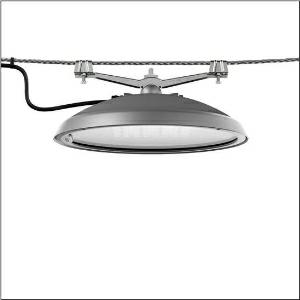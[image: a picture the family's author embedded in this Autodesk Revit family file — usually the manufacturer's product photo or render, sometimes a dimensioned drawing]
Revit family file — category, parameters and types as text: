
# Revit family: dl_r__50_iq_mini___st1_0s_5xa248w41f08re_89db
name_source: partatom
category: Lighting Fixtures
units: mm (PartAtom-declared; Revit-internal decimal feet)

## family parameters
Cut with Voids When Loaded = No
Host = Face
Light Source = No
Part Type = Normal
Room Calculation Point = No
Round Connector Dimension = Use Diameter
Shared = No

## types (1)
- --- (1 x LED, 5990 lm, 33.8 W, 4000K)
    Apparent Load = 34 VA
    CIE Flux Codes = 37 72 97 100 100
    Color Rendering = 70
    Color Temperature = 4000K
    Default Elevation = 1800 mm
    Description = DL® 50 iQ mini, catenary luminaire, primary light control with lens, of PMMA, primary optical cover: cover, of toughened safety glass, transparent, light distribution: ST1.0s, light emission: direct distribution, primary light characteristic: symmetric, installation type: suspended mounting, LED, High Power LED, rated luminous flux: 5.990lm, luminous efficacy: 177lm/W, light colour: 740, colour temperature: 4000K, control gear: iQ Street-Remote, control: optimised constant luminous flux control (CLO 2.0), Desk-Remote (wireless, voltage-free reading and setting of iQ features in the workshop via application-optimized NFC function/RFID function), Light-Fading, Smart-Wire, Night-Set, Lumen-Switch, Temp-Guard, Auto-Match, Street-Remote, mains connection: 230..240V, AC, 50/60Hz, start of lifetime: 34W, end of service life: 35W, reduction: 16W, luminaire housing, of diecast aluminium, powder-coated, Siteco® metallic grey (DB 702S), diameter: 500mm, height: 115mm, mounting height: 4..12m, protection rating (complete): IP66, insulation class (complete): insulation class II (safety insulation), certification: CE, ENEC, ENEC+, VDE, impact resistance: IK08, permissible operating ambient temperature for outdoor applications: -25..+40°C, standard-compliant lighting for roads and squares, packaging unit: 1 piece

Light Distribution: ST1.0s
    Height = 124 mm  [stored 0.406824 ft]
    Lamp = 1 x LED
    Lamp Light Flux = 5990 lm
    Lamp Power = 33.8 W
    Lamp count = 1
    Length = 500 mm
    Luminous efficacy = 177 lm/W
    Manufacturer = Siteco
    ModVariant = No
    Model = 5XA248W41F08RE
    Number of Poles = 1
    OnlyDefault = Yes
    Power Factor = 1
    Product Name = DL® 50 iQ mini | ST1.0s
    Product group = catenary luminaire
    ProductGroupID = 6300
    Protection Class = Protection class II
    Protection Degree = IP 66
    RLX_Detail_Level = 1
    RLX_Emergency_Light_Flux = 0 lm
    RLX_Emergency_Type = 0
    RLX_Emergency_Type_DB = No
    RlxData = <blob elided: 123845 chars, md5=371a3253>
    Socket = socket
    Standby Power = 0 W
    System Light Flux = 5990 lm
    System Power = 34 W
    Type Comments = factory setting: luminous flux: 100 % | dim-lin: 254 | 359 mA
    Type Image = l_1242791.jpg
    URL = http://relux.com
    VarID = @adj_140716
    Voltage = 0 V
    Weight = 0.00 kg
    Width = 0 mm  [stored 0 ft]

note: [stored X ft] marks values corroborated as IEEE doubles in the binary element streams (Revit-internal decimal feet)

## geometry (parser evidence)
native form markers: Blend x4, Sweep x12
no freeform markers — native parametric forms only
